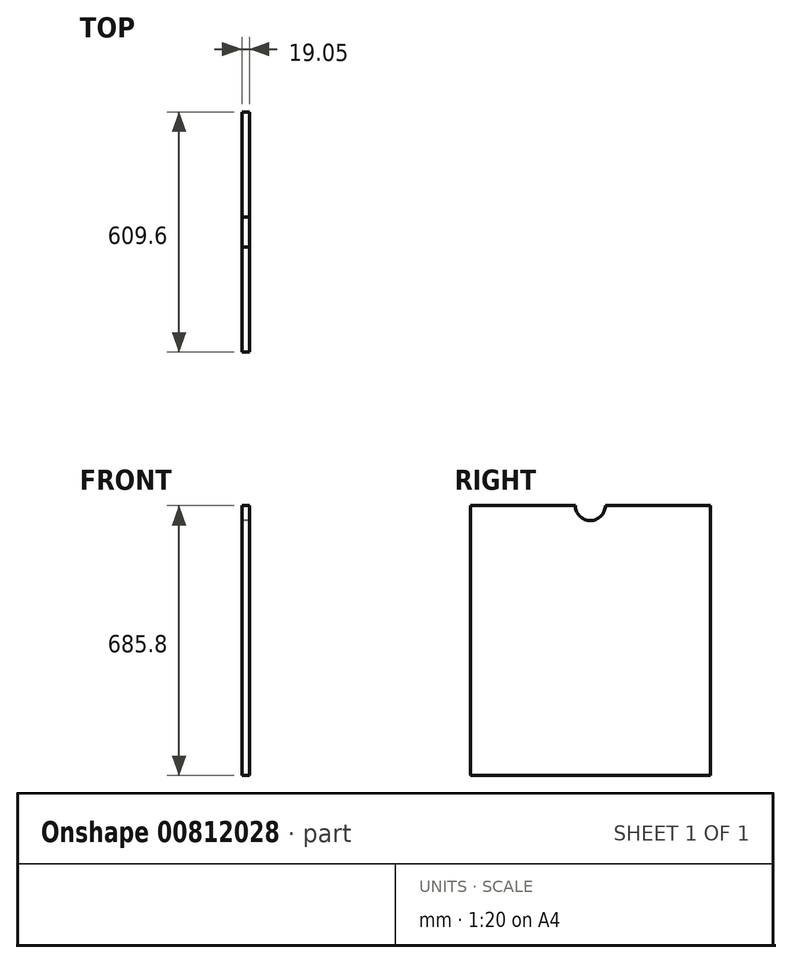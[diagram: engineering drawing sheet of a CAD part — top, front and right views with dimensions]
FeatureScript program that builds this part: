
annotation { "Feature Type Name" : "Feature", "Feature Type Description" : "" }
export const myFeature = defineFeature(function(context is Context, id is Id, definition is map)
    precondition{}
    {
        {
            var Q0;
            Q0=qCreatedBy(makeId("Right.planeOp"),FACE);
            var sketch = newSketch(context, id + "F0", { "sketchPlane" : qUnion([Q0])});
            skLineSegment(sketch, "E0.bottom", {"start": v(-304.8, 342.9) * mm, "end": v(304.8, 342.9) * mm});
            skLineSegment(sketch, "E0.top", {"start": v(-304.8, -342.9) * mm, "end": v(304.8, -342.9) * mm});
            skLineSegment(sketch, "E0.left", {"start": v(-304.8, 342.9) * mm, "end": v(-304.8, -342.9) * mm});
            skLineSegment(sketch, "E0.right", {"start": v(304.8, 342.9) * mm, "end": v(304.8, -342.9) * mm});
            skPoint(sketch, "E0.middle", {"position": v(0, 0) * mm});
            skCircle(sketch, "E1", {"center": v(0, 342.9) * mm, "radius": 38.1 * mm});
            skSolve(sketch);
        }
        {
            var Q0;
            Q0=makeQuery(id+"F0.imprint","IMPRINT",FACE,{"disambiguationData":[TD([[makeQuery(id+"F0.imprint","IMPRINT",EDGE,{"derivedFrom":sQuery(id+"F0.wireOp",EDGE,"E0.top")}),1.0]])]});
            extrude(context, id + "F1", {"entities" : qUnion([Q0]), "depth" : 19.05 * mm, "offsetDistance" : 25.4 * mm});
        }
    });
